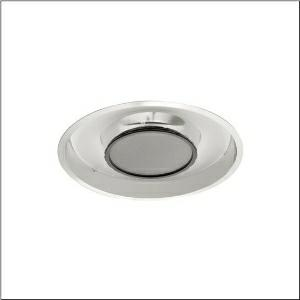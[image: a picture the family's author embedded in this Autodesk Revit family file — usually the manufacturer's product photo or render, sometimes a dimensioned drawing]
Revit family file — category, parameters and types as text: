
# Revit family: lunis_11_r_5lr610d4ob11af
name_source: partatom
category: Lighting Fixtures
units: mm (PartAtom-declared; Revit-internal decimal feet)

## family parameters
Cut with Voids When Loaded = No
Host = Face
Light Source = No
Part Type = Normal
Room Calculation Point = No
Round Connector Dimension = Use Diameter
Shared = No

## types (1)
- --- (1 x LED 4000K / CRI = 80 (unbekannt), 4860 lm, 4000K)
    Apparent Load = 37 VA
    CIE Flux Codes = 60 90 99 100 100
    Color Rendering = 80
    Color Temperature = 4000K
    Default Elevation = 1800 mm
    Description = Lunis 11 R, downlight, light control with reflector, of ultra-pure aluminium (Al 99.98%), highly specular, perforated, light emission: direct distribution, LED rated luminous flux: 4.860lm, light colour: 840, control gear: ECG Multilumen, with terminal, 3+2-pole, max. 2.5mm², mains connection: 230V, AC, 50/60Hz, diameter: 398mm, central ring, of plastic, graphite (RAL 7037), central module, blanking cover, of sheet steel, perforated, metallic grey (RAL 9006), protection rating (complete): IP20, insulation class (complete): insulation class II (safety insulation), certification: CE, ENEC, VDE, protection symbol: F, permissible ambient temperature for indoor applications: +10..+35°C, standard: EN 50419, packaging unit: 1 piece
    Height = 0 mm  [stored 0 ft]
    Lamp = 1 x LED 4000K / CRI >= 80 (unbekannt)
    Lamp Light Flux = 4860 lm
    Lamp count = 1
    Length = 398 mm
    Luminous efficacy = 131 lm/W
    Manufacturer = Siteco
    ModVariant = No
    Model = 5LR610D4OB11AF
    Mounting Place = Ceiling
    Mounting Type = Recessed
    Number of Poles = 1
    OnlyDefault = Yes
    Power Factor = 1
    Product Name = Lunis 11 R
    Product group = downlight
    ProductGroupID = 400
    Protection Class = Protection class II
    Protection Degree = IP 20
    RLX_Detail_Level = 1
    RLX_Emergency_Light_Flux = 0 lm
    RLX_Emergency_Type = 0
    RLX_Emergency_Type_DB = No
    RlxData = <blob elided: 94297 chars, md5=744dd51f>
    Socket = socket
    Standby Power = 0 W
    System Light Flux = 4860 lm
    System Power = 37 W
    Type Comments = factory setting: High Lumen Output
    Type Image = l_1003323.jpg
    URL = http://relux.com
    VarID = @adj_202872
    Voltage = 0 V
    Weight = 0.00 kg
    Width = 0 mm  [stored 0 ft]

note: [stored X ft] marks values corroborated as IEEE doubles in the binary element streams (Revit-internal decimal feet)

## geometry (parser evidence)
native form markers: Blend x4, Sweep x9
no freeform markers — native parametric forms only
